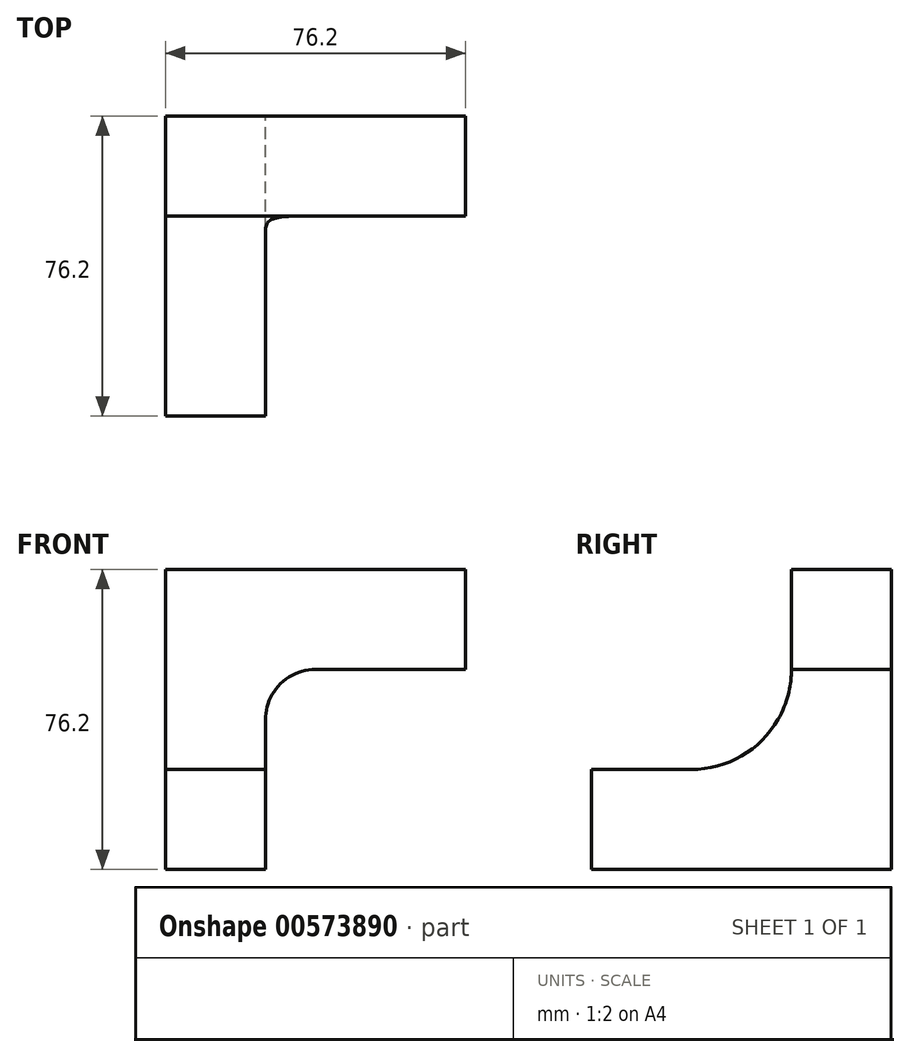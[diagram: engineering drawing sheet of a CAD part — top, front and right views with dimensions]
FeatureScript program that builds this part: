
annotation { "Feature Type Name" : "Feature", "Feature Type Description" : "" }
export const myFeature = defineFeature(function(context is Context, id is Id, definition is map)
    precondition{}
    {
        {
            var Q0;
            Q0=qCreatedBy(makeId("Front.planeOp"),FACE);
            var sketch = newSketch(context, id + "F0", { "sketchPlane" : qUnion([Q0])});
            skLineSegment(sketch, "E0", {"start": v(0, 0) * mm, "end": v(0, 76.2) * mm});
            skLineSegment(sketch, "E1", {"start": v(0, 76.2) * mm, "end": v(76.2, 76.2) * mm});
            skLineSegment(sketch, "E2", {"start": v(76.2, 76.2) * mm, "end": v(76.2, 50.8) * mm});
            skLineSegment(sketch, "E3", {"start": v(76.2, 50.8) * mm, "end": v(38.1, 50.8) * mm});
            skLineSegment(sketch, "E4", {"start": v(25.4, 38.1) * mm, "end": v(25.4, 0) * mm});
            skLineSegment(sketch, "E5", {"start": v(25.4, 0) * mm, "end": v(0, 0) * mm});
            skPoint(sketch, "E6.visualSharp", {"position": v(25.4, 50.8) * mm});
            skArc(sketch, "E6.filletArc", {"start": v(38.1, 50.8) * mm, "mid": v(29.12, 47.08) * mm, "end": v(25.4, 38.1) * mm});
            skSolve(sketch);
        }
        {
            var Q0;
            Q0 = qSketchRegion(id + "F0", true);
            extrude(context, id + "F1", {"entities" : qUnion([Q0]), "depth" : 76.2 * mm, "offsetDistance" : 25.4 * mm});
        }
        {
            var Q0;
            Q0=makeQuery(id+"F1.opExtrude","SWEPT_FACE",FACE,{"disambiguationData":[OSD([sQuery(id+"F0.wireOp",EDGE,"E2")])]});
            var sketch = newSketch(context, id + "F2", { "sketchPlane" : qUnion([Q0])});
            skLineSegment(sketch, "E7", {"start": v(-76.2, 25.4) * mm, "end": v(-50.8, 25.4) * mm});
            skLineSegment(sketch, "E8", {"start": v(-25.4, 50.8) * mm, "end": v(-25.4, 76.2) * mm});
            skLineSegment(sketch, "E9", {"start": v(-25.4, 76.2) * mm, "end": v(-76.2, 76.2) * mm});
            skLineSegment(sketch, "E10", {"start": v(-76.2, 76.2) * mm, "end": v(-76.2, 25.4) * mm});
            skPoint(sketch, "E11.visualSharp", {"position": v(-25.4, 25.4) * mm});
            skArc(sketch, "E11.filletArc", {"start": v(-50.8, 25.4) * mm, "mid": v(-32.84, 32.84) * mm, "end": v(-25.4, 50.8) * mm});
            skSolve(sketch);
        }
        {
            var Q0;
            Q0 = qSketchRegion(id + "F2", true);
            extrude(context, id + "F3", {"entities" : qUnion([Q0]), "operationType" : NewBodyOperationType.REMOVE, "endBound" : BoundingType.THROUGH_ALL, "oppositeDirection" : true, "depth" : 25.4 * mm, "offsetDistance" : 25.4 * mm});
        }
    });
